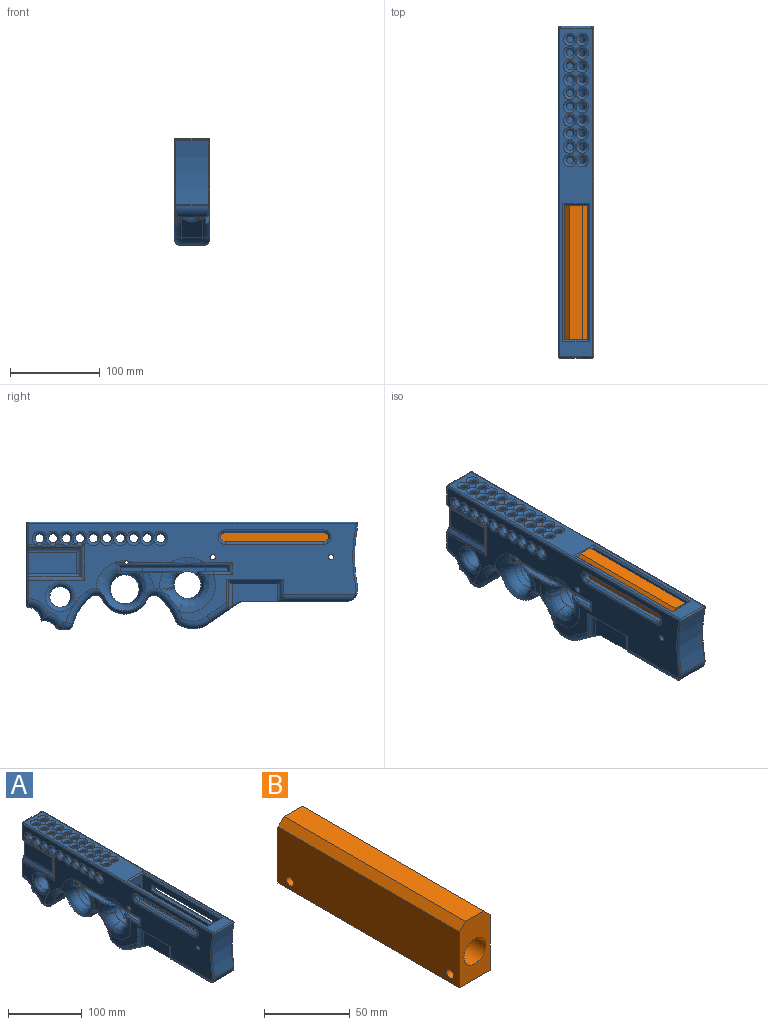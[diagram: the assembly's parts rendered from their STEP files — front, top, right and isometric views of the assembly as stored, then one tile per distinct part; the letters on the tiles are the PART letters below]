
ASSEMBLY  parts=2 mates=1
PART A: 322 faces, bbox 46.1x384.5x124.3 mm
  f0: plane 7.63x4.32mm, normal (-1,0,0), area 12.3mm2, adj f99,f284,f287
  f1: plane 7.63x4.32mm, normal (-1,0,0), area 12.3mm2, adj f99,f287,f289
  f2: plane 365.05x110.05mm, normal (-1,0,0), area 16579.4mm2, adj f26,f27,f29,f35,f58,f62,f64,f69
  f3: plane 7.63x4.32mm, normal (1,0,0), area 12.3mm2, adj f103,f269,f272
  f4: plane 7.63x4.32mm, normal (1,0,0), area 12.3mm2, adj f103,f267,f269
  f5: plane 7.63x4.32mm, normal (1,0,0), area 12.3mm2, adj f103,f265,f267
  f6: cylinder r=4mm len=2.6mm, axis (0,0,1), area 2.6mm2, adj f134,f261
  f7: cylinder r=4mm len=2.6mm, axis (0,0,1), area 2.9mm2, adj f134,f258
  f8: cylinder r=4mm len=2.6mm, axis (0,0,1), area 2.9mm2, adj f134,f253
  f9: cylinder r=4mm len=2.6mm, axis (0,0,1), area 2.9mm2, adj f134,f256
  f10: cylinder r=4mm len=2.6mm, axis (0,0,1), area 2.6mm2, adj f134,f255
  f11: cylinder r=4mm len=2.6mm, axis (0,0,1), area 2.6mm2, adj f134,f262
  f12: cylinder r=4mm len=2.6mm, axis (0,0,1), area 2.6mm2, adj f134,f262
  f13: cylinder r=4mm len=2.6mm, axis (0,0,1), area 2.6mm2, adj f134,f259
  f14: cylinder r=4mm len=2.6mm, axis (0,0,1), area 2.6mm2, adj f134,f261
  f15: cylinder r=4mm len=2.6mm, axis (0,0,1), area 2.6mm2, adj f134,f260
  f16: cylinder r=4mm len=2.6mm, axis (0,0,1), area 2.6mm2, adj f134,f260
  f17: cylinder r=4mm len=2.6mm, axis (0,0,1), area 2.6mm2, adj f134,f259
  f18: cylinder r=4mm len=2.6mm, axis (0,0,1), area 2.9mm2, adj f134,f257
  f19: cylinder r=4mm len=2.6mm, axis (0,0,1), area 2.9mm2, adj f134,f258
  f20: cylinder r=4mm len=2.6mm, axis (0,0,1), area 2.9mm2, adj f134,f257
  f21: cylinder r=4mm len=2.6mm, axis (0,0,1), area 2.9mm2, adj f134,f256
  f22: cylinder r=4mm len=2.6mm, axis (0,0,1), area 2.6mm2, adj f134,f255
  f23: cylinder r=4mm len=2.6mm, axis (0,0,1), area 2.6mm2, adj f134,f254
  f24: cylinder r=4mm len=2.6mm, axis (0,0,1), area 2.6mm2, adj f134,f254
  f25: cylinder r=4mm len=2.6mm, axis (0,0,1), area 2.9mm2, adj f134,f253
  f26: bspline ~11.72x3.95mm, area 18.6mm2, adj f2,f27,f244,f249
  f27: bspline ~63.97x63.94mm, area 2302.5mm2, adj f2,f26,f30,f44,f74,f78,f82,f224
  f28: plane 7.63x4.32mm, normal (-1,0,0), area 12.3mm2, adj f99,f289,f291
  f29: bspline ~8.66x3.85mm, area 8.2mm2, adj f2,f244,f249
  f30: cylinder r=16mm len=32mm, axis (1,0,0), area 557.5mm2, adj f27,f31,f227,f228
  f31: bspline ~63.97x63.93mm, area 2680.9mm2, adj f30,f47,f68,f71,f75,f226,f227,f228
  f32: plane 68.15x14.42mm, normal (0,0,1), area 729.7mm2, adj f34,f223,f224,f225,f240,f241,f242,f243
  f33: plane 120.04x10.01mm, normal (0,0,-1), area 932.2mm2, adj f34,f36,f37,f222,f223,f224,f225,f243
  f34: plane 6.87x5mm, normal (0,-1,0), area 28.1mm2, adj f32,f33,f224,f243
  f35: bspline ~61.97x61.95mm, area 1778mm2, adj f2,f44,f53,f92,f93,f223,f238,f242
  f36: plane 55x25mm, normal (0,-1,0), area 807.4mm2, adj f33,f37,f39,f133,f134,f203,f208,f209
  f37: plane 150x55mm, normal (1,0,0), area 6889.9mm2, adj f33,f36,f132,f200,f202,f204,f209,f217
  f38: torus R=16mm, axis (1,0,0), area 15.4mm2, adj f58,f59,f62,f181
  f39: plane 150x15mm, normal (0,0,1), area 1672.7mm2, adj f36,f132,f133,f207,f208,f210,f211,f212
  f40: plane 29.98x24.03mm, normal (0,-0.57,-0.82), area 805.6mm2, adj f41,f50,f59,f60,f62,f190
  f41: cylinder r=8mm len=4.58mm, axis (-1,0,0), area 12.7mm2, adj f40,f52,f57,f191,f192
  f42: plane 365.3x36mm, normal (0,0,1), area 5606.1mm2, adj f114,f130,f131,f155,f156,f157,f158,f159
  f43: plane 36x0.93mm, normal (0,-1,0), area 33.5mm2, adj f113,f114,f126,f127
  f44: plane 19.37x17mm, normal (-1,0,0), area 178.3mm2, adj f27,f35,f74,f241
  f45: plane 24x5.45mm, normal (0,0,-1), area 128.8mm2, adj f73,f77,f80,f81,f87,f90
  f46: plane 22.3x0.17mm, normal (0,0.53,-0.85), area 3.6mm2, adj f54,f55,f85,f86,f88,f89
  f47: plane 365.04x110.04mm, normal (1,0,0), area 17645.4mm2, adj f31,f56,f60,f61,f66,f68,f72,f73
  f48: cylinder r=60mm len=30.99mm, axis (1,0,0), area 905.4mm2, adj f72,f79,f80,f84
  f49: cylinder r=27.5mm len=50.29mm, axis (1,0,0), area 1523.1mm2, adj f70,f71,f78,f79
  f50: cylinder r=30mm len=36.83mm, axis (1,0,0), area 955.6mm2, adj f40,f61,f64,f65
  f51: cylinder r=60mm len=26.94mm, axis (1,0,0), area 803.4mm2, adj f65,f66,f69,f70
  f52: plane 114.89x24mm, normal (0,0,-1), area 1402.5mm2, adj f41,f56,f58,f59,f115,f185,f187,f189
  f53: cylinder r=15mm len=30mm, axis (1,0,0), area 780.5mm2, adj f35,f92,f93,f94,f95,f96
  f54: cylinder r=15mm len=20mm, axis (1,0,0), area 454.3mm2, adj f46,f85,f88,f307
  f55: cylinder r=15mm len=20mm, axis (1,0,0), area 355.1mm2, adj f46,f77,f86,f89
  f56: cylinder r=8mm len=125.28mm, axis (0,1,0), area 1098.9mm2, adj f47,f52,f57,f116,f182,f183
  f57: torus R=16mm, axis (1,0,0), area 15.4mm2, adj f41,f56,f60,f183
  f58: cylinder r=8mm len=125.28mm, axis (0,1,0), area 1089.5mm2, adj f2,f38,f52,f117,f181,f196
  f59: cylinder r=8mm len=4.58mm, axis (-1,0,0), area 12.7mm2, adj f38,f40,f52,f186,f188
  f60: cylinder r=8mm len=35.02mm, axis (0,0.82,-0.57), area 362.2mm2, adj f40,f47,f57,f61,f183,f184
  f61: torus R=22mm, axis (1,0,0), area 455.6mm2, adj f47,f50,f60,f63
  f62: cylinder r=8mm len=35.02mm, axis (0,0.82,-0.57), area 338mm2, adj f2,f38,f40,f64,f181,f198
  f63: sphere r=8mm, area 29mm2, adj f61,f65,f66
  f64: torus R=22mm, axis (1,0,0), area 455.6mm2, adj f2,f50,f62,f67
  f65: cylinder r=8mm len=24mm, axis (-1,0,0), area 125.2mm2, adj f50,f51,f63,f67
  f66: torus R=68mm, axis (1,0,0), area 441mm2, adj f47,f51,f63,f68,f96
  f67: sphere r=8mm, area 29mm2, adj f64,f65,f69
  f68: torus R=16mm, axis (1,0,0), area 211.9mm2, adj f31,f47,f66,f70,f71,f95
  f69: torus R=68mm, axis (1,0,0), area 441mm2, adj f2,f51,f67,f74,f92
  f70: cylinder r=8mm len=24mm, axis (1,0,0), area 351mm2, adj f49,f51,f68,f74
  f71: torus R=19.5mm, axis (1,0,0), area 473.4mm2, adj f31,f49,f68,f75
  f72: torus R=68mm, axis (1,0,0), area 497mm2, adj f47,f48,f75,f76
  f73: cylinder r=8mm len=8mm, axis (0,-1,0), area 38.6mm2, adj f45,f47,f76,f90
  f74: torus R=16mm, axis (1,0,0), area 211.9mm2, adj f27,f44,f69,f70,f78,f93
  f75: torus R=16mm, axis (1,0,0), area 211.9mm2, adj f31,f47,f71,f72,f79
  f76: sphere r=8mm, area 83.4mm2, adj f72,f73,f80
  f77: cylinder r=8mm len=20mm, axis (1,0,0), area 155.2mm2, adj f45,f55,f87,f90
  f78: torus R=19.5mm, axis (1,0,0), area 473.4mm2, adj f27,f49,f74,f82
  f79: cylinder r=8mm len=24mm, axis (1,0,0), area 351mm2, adj f48,f49,f75,f82
  f80: cylinder r=8mm len=24mm, axis (1,0,0), area 250.2mm2, adj f45,f48,f76,f83
  f81: cylinder r=8mm len=8mm, axis (0,1,0), area 38.6mm2, adj f2,f45,f83,f87
  f82: torus R=16mm, axis (1,0,0), area 211.9mm2, adj f2,f27,f78,f79,f84
  f83: sphere r=8mm, area 87.1mm2, adj f80,f81,f84
  f84: torus R=68mm, axis (1,0,0), area 497mm2, adj f2,f48,f82,f83
  f85: torus R=25mm, axis (1,0,0), area 385.5mm2, adj f2,f46,f54,f86,f305
  f86: torus R=25mm, axis (1,0,0), area 294.6mm2, adj f2,f46,f55,f85,f87
  f87: bspline ~11.65x10.38mm, area 96.3mm2, adj f45,f77,f81,f86
  f88: torus R=25mm, axis (1,0,0), area 385.5mm2, adj f46,f47,f54,f89,f309
  f89: torus R=25mm, axis (1,0,0), area 294.6mm2, adj f46,f47,f55,f88,f90
  f90: bspline ~11.78x10.06mm, area 96.3mm2, adj f45,f73,f77,f89
  f91: bspline ~36.66x6mm, area 0.1mm2, adj f2,f247
  f92: bspline ~26.53x23.21mm, area 387.1mm2, adj f35,f53,f69,f93
  f93: bspline ~16.3x16mm, area 44.2mm2, adj f35,f53,f74,f92
  f94: bspline ~61.97x61.95mm, area 2749.4mm2, adj f47,f53,f95,f96
  f95: bspline ~16.3x16mm, area 44.2mm2, adj f53,f68,f94,f96
  f96: bspline ~26.53x23.21mm, area 387mm2, adj f53,f66,f94,f95
  f97: plane 48.75x23.5mm, normal (1,0,0), area 1145.4mm2, adj f108,f109,f110,f317
  f98: plane 53.75x23.5mm, normal (-1,0,0), area 1262.9mm2, adj f105,f106,f107,f304
  f99: bspline ~77.4x4.9mm, area 245.2mm2, adj f0,f1,f2,f28,f101,f105,f281,f283
  f100: bspline ~77.4x4.9mm, area 277.3mm2, adj f2,f101,f106,f301
  f101: bspline ~41.33x4.9mm, area 166.2mm2, adj f2,f99,f100,f107
  f102: bspline ~42.45x4.9mm, area 164mm2, adj f47,f103,f104,f108,f270,f271
  f103: bspline ~72.23x4.9mm, area 226.9mm2, adj f3,f4,f5,f47,f102,f109,f264,f266
  f104: bspline ~72.23x4.9mm, area 254.2mm2, adj f47,f102,f110,f313
  f105: cylinder r=5mm len=57.87mm, axis (0,1,0), area 269.9mm2, adj f98,f99,f107,f306
  f106: cylinder r=5mm len=57.87mm, axis (0,-1,0), area 269.9mm2, adj f98,f100,f107,f302
  f107: cylinder r=5mm len=31.73mm, axis (0,0,1), area 133.6mm2, adj f98,f101,f105,f106
  f108: cylinder r=5mm len=31.73mm, axis (0,0,1), area 133.6mm2, adj f97,f102,f109,f110
  f109: cylinder r=5mm len=52.87mm, axis (0,1,0), area 245.7mm2, adj f97,f103,f108,f319
  f110: cylinder r=5mm len=52.87mm, axis (0,-1,0), area 245.7mm2, adj f97,f104,f108,f315
  f111: cylinder r=166.9mm len=71.34mm, axis (1,0,0), area 2588.3mm2, adj f112,f113,f122,f123
  f112: bspline ~44x0.36mm, area 12.9mm2, adj f111,f115,f120,f121
  f113: bspline ~44x0.36mm, area 13.2mm2, adj f43,f111,f124,f125
  f114: bspline ~44x1.7mm, area 99.3mm2, adj f42,f43,f128,f129
  f115: cylinder r=14mm len=36mm, axis (-1,0,0), area 702.8mm2, adj f52,f112,f116,f117,f118,f119
  f116: bspline ~12.98x9.58mm, area 18.5mm2, adj f56,f115,f118
  f117: bspline ~12.98x9.58mm, area 18.6mm2, adj f58,f115,f119
  f118: torus R=12mm, axis (1,0,0), area 21.7mm2, adj f47,f115,f116,f120
  f119: torus R=12mm, axis (1,0,0), area 21.7mm2, adj f2,f115,f117,f121
  f120: bspline ~2.45x2mm, area 0.5mm2, adj f112,f118,f122
  f121: bspline ~2.45x2mm, area 0.5mm2, adj f112,f119,f123
  f122: torus R=168.9mm, axis (1,0,0), area 226.8mm2, adj f47,f111,f120,f124
  f123: torus R=168.9mm, axis (1,0,0), area 226.8mm2, adj f2,f111,f121,f125
  f124: bspline ~2.11x2mm, area 0.5mm2, adj f113,f122,f126
  f125: bspline ~2.11x2mm, area 0.5mm2, adj f113,f123,f127
  f126: cylinder r=2mm len=2mm, axis (0,0,1), area 2.4mm2, adj f43,f47,f124,f128
  f127: cylinder r=2mm len=2mm, axis (0,0,-1), area 2.4mm2, adj f2,f43,f125,f129
  f128: bspline ~2x2mm, area 3.5mm2, adj f114,f126,f130
  f129: bspline ~2x2mm, area 3.5mm2, adj f114,f127,f131
  f130: cylinder r=2mm len=365.3mm, axis (0,1,0), area 1147.2mm2, adj f42,f47,f128,f316
  f131: cylinder r=2mm len=365.3mm, axis (0,-1,0), area 1147.2mm2, adj f2,f42,f129,f312
  f132: plane 55x25mm, normal (0,1,0), area 1195mm2, adj f37,f39,f133,f206,f207,f209
  f133: plane 150x43mm, normal (-1,0,0), area 5214.9mm2, adj f36,f39,f132,f199,f201,f205,f213,f214
  f134: cylinder r=11mm len=197mm, axis (0,-1,0), area 11117.8mm2, adj f6,f7,f8,f9,f10,f11,f12,f13
  f135: cylinder r=4mm len=10mm, axis (0,0,1), area 251.3mm2, adj f174,f261
  f136: cylinder r=4mm len=10mm, axis (0,0,1), area 251.3mm2, adj f155,f258
  f137: cylinder r=4mm len=10mm, axis (0,0,1), area 251.3mm2, adj f156,f253
  f138: cylinder r=4mm len=10mm, axis (0,0,1), area 251.3mm2, adj f157,f256
  f139: cylinder r=4mm len=10mm, axis (0,0,1), area 251.3mm2, adj f166,f255
  f140: cylinder r=4mm len=10mm, axis (0,0,1), area 251.3mm2, adj f167,f262
  f141: cylinder r=4mm len=10mm, axis (0,0,1), area 251.3mm2, adj f168,f262
  f142: cylinder r=4mm len=10mm, axis (0,0,1), area 251.3mm2, adj f169,f259
  f143: cylinder r=4mm len=10mm, axis (0,0,1), area 251.3mm2, adj f173,f261
  f144: cylinder r=4mm len=10mm, axis (0,0,1), area 251.3mm2, adj f172,f260
  f145: cylinder r=4mm len=10mm, axis (0,0,1), area 251.3mm2, adj f171,f260
  f146: cylinder r=4mm len=10mm, axis (0,0,1), area 251.3mm2, adj f170,f259
  f147: cylinder r=4mm len=10mm, axis (0,0,1), area 251.3mm2, adj f158,f257
  f148: cylinder r=4mm len=10mm, axis (0,0,1), area 251.3mm2, adj f159,f258
  f149: cylinder r=4mm len=10mm, axis (0,0,1), area 251.3mm2, adj f160,f257
  f150: cylinder r=4mm len=10mm, axis (0,0,1), area 251.3mm2, adj f161,f256
  f151: cylinder r=4mm len=10mm, axis (0,0,1), area 251.3mm2, adj f165,f255
  f152: cylinder r=4mm len=10mm, axis (0,0,1), area 251.3mm2, adj f164,f254
  f153: cylinder r=4mm len=10mm, axis (0,0,1), area 251.3mm2, adj f163,f254
  f154: cylinder r=4mm len=10mm, axis (0,0,1), area 251.3mm2, adj f162,f253
  f155: torus R=7mm, axis (0,0,1), area 150.7mm2, adj f42,f136
  f156: torus R=7mm, axis (0,0,1), area 150.7mm2, adj f42,f137
  f157: torus R=7mm, axis (0,0,1), area 150.7mm2, adj f42,f138
  f158: torus R=7mm, axis (0,0,1), area 150.7mm2, adj f42,f147
  f159: torus R=7mm, axis (0,0,1), area 150.7mm2, adj f42,f148
  f160: torus R=7mm, axis (0,0,1), area 150.7mm2, adj f42,f149
  f161: torus R=7mm, axis (0,0,1), area 150.7mm2, adj f42,f150
  f162: torus R=7mm, axis (0,0,1), area 150.7mm2, adj f42,f154
  f163: torus R=7mm, axis (0,0,1), area 150.7mm2, adj f42,f153
  f164: torus R=7mm, axis (0,0,1), area 150.7mm2, adj f42,f152
  f165: torus R=7mm, axis (0,0,1), area 150.7mm2, adj f42,f151
  f166: torus R=7mm, axis (0,0,1), area 150.7mm2, adj f42,f139
  f167: torus R=7mm, axis (0,0,1), area 150.7mm2, adj f42,f140
  f168: torus R=7mm, axis (0,0,1), area 150.7mm2, adj f42,f141
  f169: torus R=7mm, axis (0,0,1), area 150.7mm2, adj f42,f142
  f170: torus R=7mm, axis (0,0,1), area 150.7mm2, adj f42,f146
  f171: torus R=7mm, axis (0,0,1), area 150.7mm2, adj f42,f145
  f172: torus R=7mm, axis (0,0,1), area 150.7mm2, adj f42,f144
  f173: torus R=7mm, axis (0,0,1), area 150.7mm2, adj f42,f143
  f174: torus R=7mm, axis (0,0,1), area 150.7mm2, adj f42,f135
  f175: plane 28.72x25mm, normal (1,0,0), area 716.6mm2, adj f176,f178,f185,f186,f209
  f176: cylinder r=7mm len=38.66mm, axis (0,0,1), area 752.3mm2, adj f175,f177,f187,f207,f209,f212
  f177: plane 38.72x25mm, normal (-1,0,0), area 966.6mm2, adj f176,f178,f189,f191,f211
  f178: cylinder r=7mm len=44.01mm, axis (0,0,1), area 813.6mm2, adj f175,f177,f188,f190,f192,f208,f209,f210
  f179: cylinder r=5mm len=21.49mm, axis (0,0,-1), area 102.7mm2, adj f181,f193,f195,f196
  f180: cylinder r=5mm len=29.57mm, axis (0,0,-1), area 178.5mm2, adj f181,f193,f197,f198
  f181: plane 54.19x23.78mm, normal (-1,0,0), area 993.5mm2, adj f38,f58,f62,f179,f180,f193,f196,f198
  f182: cylinder r=5mm len=24.42mm, axis (0,0,-1), area 143mm2, adj f47,f56,f183,f194
  f183: plane 50x25.29mm, normal (1,0,0), area 996.2mm2, adj f56,f57,f60,f182,f184,f194
  f184: cylinder r=5mm len=30.29mm, axis (0,0,-1), area 196.4mm2, adj f47,f60,f183,f194
  f185: plane 23.89x3mm, normal (0.71,0,-0.71), area 101.3mm2, adj f52,f175,f186,f187
  f186: cone r=8mm half-angle=45deg, axis (1,0,0), area 4.1mm2, adj f59,f175,f185,f188
  f187: cone r=7mm half-angle=45deg, axis (0,0,-1), area 113.3mm2, adj f52,f176,f185,f189
  f188: bspline ~4.38x4.02mm, area 17.3mm2, adj f59,f178,f186,f190
  f189: plane 23.89x3mm, normal (-0.71,0,-0.71), area 101.3mm2, adj f52,f177,f187,f191
  f190: bspline ~17.11x5.82mm, area 58.4mm2, adj f40,f178,f188,f192
  f191: cone r=11mm half-angle=45deg, axis (-1,0,0), area 4.1mm2, adj f41,f177,f189,f192
  f192: bspline ~4.38x4.02mm, area 17.3mm2, adj f41,f178,f190,f191
  f193: plane 65.18x6.77mm, normal (-0.71,0,-0.71), area 410.1mm2, adj f2,f179,f180,f181,f195,f197
  f194: plane 62.1x7.1mm, normal (0.71,0,-0.71), area 409.1mm2, adj f47,f182,f183,f184
  f195: cylinder r=2mm len=17mm, axis (0,0,-1), area 41.7mm2, adj f2,f179,f193,f196
  f196: bspline ~8.64x7.04mm, area 25.2mm2, adj f58,f179,f181,f195
  f197: cylinder r=2mm len=25.93mm, axis (0,0,-1), area 64.6mm2, adj f2,f180,f193,f198
  f198: bspline ~12.66x8.1mm, area 34.8mm2, adj f62,f180,f181,f197
  f199: cylinder r=3mm len=7.5mm, axis (1,0,0), area 141.4mm2, adj f47,f133
  f200: cylinder r=3mm len=7.5mm, axis (1,0,0), area 141.4mm2, adj f2,f37
  f201: cylinder r=3mm len=7.5mm, axis (1,0,0), area 141.4mm2, adj f47,f133
  f202: cylinder r=3mm len=7.5mm, axis (1,0,0), area 141.4mm2, adj f2,f37
  f203: plane 29x2mm, normal (0,-0.71,0.71), area 76.4mm2, adj f36,f42,f204,f205
  f204: plane 154x2mm, normal (0.71,0,0.71), area 429.9mm2, adj f37,f42,f203,f206
  f205: plane 154x2mm, normal (-0.71,0,0.71), area 429.9mm2, adj f42,f133,f203,f206
  f206: plane 29x2mm, normal (0,0.71,0.71), area 76.4mm2, adj f42,f132,f204,f205
  f207: plane 78.14x12.03mm, normal (-1,0.02,0), area 935.3mm2, adj f39,f132,f176,f209,f212
  f208: plane 33.04x12.02mm, normal (-1,0.02,0), area 394.3mm2, adj f36,f39,f178,f209,f210
  f209: plane 150x12.5mm, normal (0,0,1), area 1469.6mm2, adj f36,f37,f132,f175,f176,f178,f207,f208
  f210: cone r=7mm half-angle=45deg, axis (0,0,1), area 37.1mm2, adj f39,f178,f208,f211
  f211: plane 25x2mm, normal (-0.71,0,0.71), area 70.7mm2, adj f39,f177,f210,f212
  f212: cone r=7mm half-angle=45deg, axis (0,0,1), area 39mm2, adj f39,f176,f207,f211
  f213: plane 110x4.5mm, normal (0,0,-1), area 495mm2, adj f133,f214,f216,f237
  f214: cylinder r=5mm len=10mm, axis (1,0,0), area 70.7mm2, adj f133,f213,f215,f236
  f215: plane 110x4.5mm, normal (0,0,1), area 495mm2, adj f133,f214,f216,f234
  f216: cylinder r=5mm len=10mm, axis (1,0,0), area 70.7mm2, adj f133,f213,f215,f235
  f217: cylinder r=5mm len=10mm, axis (1,0,0), area 70.7mm2, adj f37,f218,f220,f231
  f218: plane 110x4.5mm, normal (0,0,1), area 495mm2, adj f37,f217,f219,f230
  f219: cylinder r=5mm len=10mm, axis (1,0,0), area 70.7mm2, adj f37,f218,f220,f232
  f220: plane 110x4.5mm, normal (0,0,-1), area 495mm2, adj f37,f217,f219,f233
  f221: plane 31.98x12mm, normal (0,0,1), area 158.7mm2, adj f36,f37,f222,f223,f238,f239,f246
  f222: plane 5x2.5mm, normal (0,1,0), area 12.5mm2, adj f33,f37,f221,f246
  f223: plane 70.33x10.33mm, normal (-1,0,0), area 369.4mm2, adj f32,f33,f35,f36,f221,f225,f238,f242
  f224: plane 31.04x30.04mm, normal (1,0,0), area 564.5mm2, adj f27,f32,f33,f34,f225,f227,f228,f229
  f225: plane 31x15mm, normal (0,1,0), area 452.5mm2, adj f32,f33,f223,f224,f226,f228,f229
  f226: plane 31.04x30.04mm, normal (-1,0,0), area 689.5mm2, adj f31,f225,f227,f228,f229,f250
  f227: plane 23.64x15.13mm, normal (0,-1,0), area 352mm2, adj f27,f30,f31,f224,f226,f229
  f228: plane 15.11x4.91mm, normal (0,0,1), area 71.5mm2, adj f27,f30,f31,f224,f225,f226
  f229: plane 30x15mm, normal (0,0,-1), area 450mm2, adj f224,f225,f226,f227
  f230: cylinder r=3mm len=110mm, axis (0,1,0), area 518.4mm2, adj f2,f218,f231,f232
  f231: torus R=8mm, axis (1,0,0), area 90.2mm2, adj f2,f217,f230,f233
  f232: torus R=8mm, axis (1,0,0), area 90.2mm2, adj f2,f219,f230,f233
  f233: cylinder r=3mm len=110mm, axis (0,-1,0), area 518.4mm2, adj f2,f220,f231,f232
  f234: cylinder r=3mm len=110mm, axis (0,-1,0), area 518.4mm2, adj f47,f215,f235,f236
  f235: torus R=8mm, axis (1,0,0), area 90.2mm2, adj f47,f216,f234,f237
  f236: torus R=8mm, axis (1,0,0), area 90.2mm2, adj f47,f214,f234,f237
  f237: cylinder r=3mm len=110mm, axis (0,1,0), area 518.4mm2, adj f47,f213,f235,f236
  f238: bspline ~22.05x16.34mm, area 146.8mm2, adj f35,f221,f223,f239
  f239: cylinder r=3mm len=21.42mm, axis (0,-1,0), area 90.1mm2, adj f2,f221,f238,f246
  f240: bspline ~36.36x6.96mm, area 72.5mm2, adj f27,f32,f241,f243
  f241: cylinder r=1mm len=16.6mm, axis (0,-1,0), area 26.1mm2, adj f32,f44,f240,f242
  f242: bspline ~24.18x15.35mm, area 58mm2, adj f32,f35,f223,f241
  f243: bspline ~14.63x9.73mm, area 56.4mm2, adj f27,f32,f33,f34,f240,f244
  f244: bspline ~22.06x5.08mm, area 140.7mm2, adj f26,f29,f33,f243,f245,f249
  f245: cylinder r=5mm len=40.54mm, axis (0,1,0), area 318.4mm2, adj f2,f33,f244,f247
  f246: cylinder r=5mm len=13mm, axis (0,0,1), area 62.2mm2, adj f2,f221,f222,f239,f248
  f247: bspline ~36.88x5.96mm, area 250.8mm2, adj f33,f91,f245,f248
  f248: cylinder r=5mm len=31.67mm, axis (0,1,0), area 229.1mm2, adj f2,f33,f246,f247
  f249: cylinder r=2mm len=12.5mm, axis (-1,0,0), area 156.3mm2, adj f2,f26,f29,f224,f244
  f250: cylinder r=2mm len=11.5mm, axis (-1,0,0), area 144.5mm2, adj f226,f251,f252
  f251: torus R=3mm, axis (1,0,0), area 6.7mm2, adj f47,f250,f252
  f252: bspline ~6x5.45mm, area 17.6mm2, adj f31,f250,f251
  f253: cylinder r=5mm len=34mm, axis (-1,0,0), area 532.7mm2, adj f8,f25,f134,f137,f154,f264,f265,f281
  f254: cylinder r=5mm len=34mm, axis (-1,0,0), area 532.1mm2, adj f23,f24,f134,f152,f153,f274,f290
  f255: cylinder r=5mm len=34mm, axis (-1,0,0), area 532.1mm2, adj f10,f22,f134,f139,f151,f276,f288
  f256: cylinder r=5mm len=34mm, axis (-1,0,0), area 532.7mm2, adj f9,f21,f134,f138,f150,f266,f267,f283
  f257: cylinder r=5mm len=34mm, axis (-1,0,0), area 532.7mm2, adj f18,f20,f134,f147,f149,f268,f269,f286
  f258: cylinder r=5mm len=34mm, axis (-1,0,0), area 532.6mm2, adj f7,f19,f134,f136,f148,f270,f271,f272
  f259: cylinder r=5mm len=34mm, axis (-1,0,0), area 532.1mm2, adj f13,f17,f134,f142,f146,f277,f282
  f260: cylinder r=5mm len=34mm, axis (-1,0,0), area 532.1mm2, adj f15,f16,f134,f144,f145,f273,f279
  f261: cylinder r=5mm len=34mm, axis (-1,0,0), area 532.1mm2, adj f6,f14,f134,f135,f143,f275,f280
  f262: cylinder r=5mm len=34mm, axis (-1,0,0), area 532.1mm2, adj f11,f12,f134,f140,f141,f278,f285
  f263: cylinder r=11.5mm len=30mm, axis (-1,0,0), area 2167.7mm2, adj f293,f294
  f264: bspline ~10.38x4.98mm, area 31mm2, adj f103,f253,f265
  f265: torus R=8mm, axis (1,0,0), area 151mm2, adj f5,f47,f253,f264,f267
  f266: bspline ~10.38x4.98mm, area 31mm2, adj f103,f256,f267
  f267: torus R=8mm, axis (1,0,0), area 149.1mm2, adj f4,f5,f47,f256,f265,f266,f269
  f268: bspline ~10.38x4.98mm, area 31mm2, adj f103,f257,f269
  f269: torus R=8mm, axis (1,0,0), area 149.1mm2, adj f3,f4,f47,f257,f267,f268,f272
  f270: bspline ~4.37x3.92mm, area 10.8mm2, adj f102,f103,f258,f271,f272
  f271: bspline ~3.13x3.1mm, area 4.3mm2, adj f102,f258,f270,f272
  f272: torus R=8mm, axis (1,0,0), area 163.2mm2, adj f3,f47,f258,f269,f270,f271,f274
  f273: torus R=8mm, axis (1,0,0), area 178.4mm2, adj f47,f260,f275
  f274: torus R=8mm, axis (1,0,0), area 176.6mm2, adj f47,f254,f272,f276
  f275: torus R=8mm, axis (1,0,0), area 176.6mm2, adj f47,f261,f273,f277
  f276: torus R=8mm, axis (1,0,0), area 176.6mm2, adj f47,f255,f274,f278
  f277: torus R=8mm, axis (1,0,0), area 176.6mm2, adj f47,f259,f275,f278
  f278: torus R=8mm, axis (1,0,0), area 176.6mm2, adj f47,f262,f276,f277
  f279: torus R=8mm, axis (1,0,0), area 178.4mm2, adj f2,f260,f280
  f280: torus R=8mm, axis (1,0,0), area 176.6mm2, adj f2,f261,f279,f282
  f281: bspline ~10.38x4.98mm, area 31mm2, adj f99,f253,f284
  f282: torus R=8mm, axis (1,0,0), area 176.6mm2, adj f2,f259,f280,f285
  f283: bspline ~10.38x4.98mm, area 31mm2, adj f99,f256,f287
  f284: torus R=8mm, axis (1,0,0), area 151mm2, adj f0,f2,f253,f281,f287
  f285: torus R=8mm, axis (1,0,0), area 176.6mm2, adj f2,f262,f282,f288
  f286: bspline ~10.38x4.98mm, area 31mm2, adj f99,f257,f289
  f287: torus R=8mm, axis (1,0,0), area 149.1mm2, adj f0,f1,f2,f256,f283,f284,f289
  f288: torus R=8mm, axis (1,0,0), area 176.6mm2, adj f2,f255,f285,f290
  f289: torus R=8mm, axis (1,0,0), area 149.1mm2, adj f1,f2,f28,f257,f286,f287,f291
  f290: torus R=8mm, axis (1,0,0), area 176.6mm2, adj f2,f254,f288,f291
  f291: torus R=8mm, axis (1,0,0), area 149.1mm2, adj f2,f28,f258,f289,f290,f292
  f292: bspline ~10.38x4.98mm, area 31mm2, adj f99,f258,f291
  f293: torus R=16.5mm, axis (1,0,0), area 657.2mm2, adj f47,f263
  f294: torus R=16.5mm, axis (1,0,0), area 657.2mm2, adj f2,f263
  f295: plane 40x20mm, normal (-1,0,0), area 800mm2, adj f52,f296,f298,f299
  f296: plane 20x18mm, normal (0,1,0), area 360mm2, adj f52,f295,f297,f299
  f297: plane 40x20mm, normal (1,0,0), area 800mm2, adj f52,f296,f298,f299
  f298: plane 20x18mm, normal (0,-1,0), area 360mm2, adj f52,f295,f297,f299
  f299: plane 40x18mm, normal (0,0,-1), area 720mm2, adj f295,f296,f297,f298
  f300: plane 89.05x34mm, normal (0,1,0), area 2123.8mm2, adj f301,f302,f303,f304,f305,f306,f307,f308
  f301: bspline ~6.02x3.64mm, area 16.8mm2, adj f100,f300,f302,f303
  f302: torus R=8mm, axis (0,-1,0), area 27.8mm2, adj f106,f300,f301,f304
  f303: cylinder r=3mm len=20.14mm, axis (0,0,-1), area 94.9mm2, adj f2,f300,f301,f305
  f304: cylinder r=3mm len=23.5mm, axis (0,0,-1), area 110.7mm2, adj f98,f300,f302,f306
  f305: bspline ~12.25x12.23mm, area 64mm2, adj f85,f300,f303,f307
  f306: torus R=8mm, axis (0,-1,0), area 27.8mm2, adj f105,f300,f304,f308
  f307: cylinder r=3mm len=20mm, axis (1,0,0), area 89.8mm2, adj f54,f300,f305,f309
  f308: bspline ~4.77x3.64mm, area 16.8mm2, adj f99,f300,f306,f310
  f309: bspline ~12.25x12.23mm, area 64mm2, adj f88,f300,f307,f311
  f310: cylinder r=3mm len=23.1mm, axis (0,0,-1), area 106.5mm2, adj f2,f300,f308,f312
  f311: cylinder r=3mm len=20.14mm, axis (0,0,1), area 94.9mm2, adj f47,f300,f309,f313
  f312: bspline ~3.16x3mm, area 6.5mm2, adj f131,f310,f314
  f313: bspline ~5.95x3.64mm, area 16.8mm2, adj f104,f300,f311,f315
  f314: cylinder r=3mm len=36mm, axis (-1,0,0), area 164.9mm2, adj f42,f300,f312,f316
  f315: torus R=8mm, axis (0,-1,0), area 27.8mm2, adj f110,f300,f313,f317
  f316: bspline ~3.16x3mm, area 6.5mm2, adj f130,f314,f318
  f317: cylinder r=3mm len=23.5mm, axis (0,0,1), area 110.7mm2, adj f97,f300,f315,f319
  f318: cylinder r=3mm len=23.1mm, axis (0,0,1), area 106.5mm2, adj f47,f300,f316,f320
  f319: torus R=8mm, axis (0,-1,0), area 27.8mm2, adj f109,f300,f317,f320
  f320: bspline ~4.8x3.64mm, area 16.8mm2, adj f103,f300,f318,f319
  f321: torus R=14mm, axis (0,-1,0), area 358mm2, adj f134,f300
PART B: 24 faces, bbox 25x150x45 mm
  f0: plane 150x15mm, normal (0,0,1), area 2250mm2, adj f4,f5,f7,f8
  f1: plane 150x40mm, normal (-1,0,0), area 5943.5mm2, adj f2,f4,f5,f8,f22,f23
  f2: plane 150x25mm, normal (0,0,-1), area 3254.2mm2, adj f1,f3,f4,f5,f14,f15,f16,f17
  f3: plane 150x40mm, normal (1,0,0), area 5943.5mm2, adj f2,f4,f5,f7,f22,f23
  f4: plane 45x25mm, normal (0,-1,0), area 845.5mm2, adj f0,f1,f2,f3,f6,f7,f8
  f5: plane 45x25mm, normal (0,1,0), area 845.5mm2, adj f0,f1,f2,f3,f6,f7,f8
  f6: cylinder r=9mm len=150mm, axis (0,-1,0), area 7780.1mm2, adj f4,f5,f10,f11,f12,f13,f14,f15
  f7: plane 150x5mm, normal (0.71,0,0.71), area 1060.7mm2, adj f0,f3,f4,f5
  f8: plane 150x5mm, normal (-0.71,0,0.71), area 1060.7mm2, adj f0,f1,f4,f5
  f9: plane 20x8mm, normal (0,0,-1), area 145.8mm2, adj f10,f11,f12,f13
  f10: plane 12x1.92mm, normal (1,0,0), area 23mm2, adj f6,f9,f11,f13
  f11: cylinder r=4mm len=8mm, axis (0,0,-1), area 19.4mm2, adj f6,f9,f10,f12
  f12: plane 12x1.94mm, normal (-1,0,0), area 23.3mm2, adj f6,f9,f11,f13
  f13: cylinder r=4mm len=7.96mm, axis (0,0,-1), area 17.3mm2, adj f6,f9,f10,f12
  f14: cylinder r=4mm len=11.94mm, axis (0,0,-1), area 137.6mm2, adj f2,f6,f15,f17
  f15: plane 12x11.94mm, normal (-1,0,0), area 143.3mm2, adj f2,f6,f14,f16
  f16: cylinder r=4mm len=11.94mm, axis (0,0,-1), area 150.5mm2, adj f2,f6,f15,f17
  f17: plane 12x11.92mm, normal (1,0,0), area 143mm2, adj f2,f6,f14,f16
  f18: plane 25x14.34mm, normal (1,0,0), area 358.6mm2, adj f2,f6,f19,f21
  f19: plane 14.34x14mm, normal (0,-1,0), area 168.2mm2, adj f2,f6,f18,f20
  f20: plane 25x14.34mm, normal (-1,0,0), area 358.6mm2, adj f2,f6,f19,f21
  f21: plane 14.34x14mm, normal (0,1,0), area 168.2mm2, adj f2,f6,f18,f20
  f22: cylinder r=3mm len=25mm, axis (1,0,0), area 471.2mm2, adj f1,f3
  f23: cylinder r=3mm len=25mm, axis (1,0,0), area 471.2mm2, adj f1,f3
PLACE A at identity
PLACE B rot(axis=(0,0,1),180deg) t=(20,20,97.5)mm
MATE fastened B.f6 <-> A.f321  axis (0,1,0) through (20,170,95)mm
